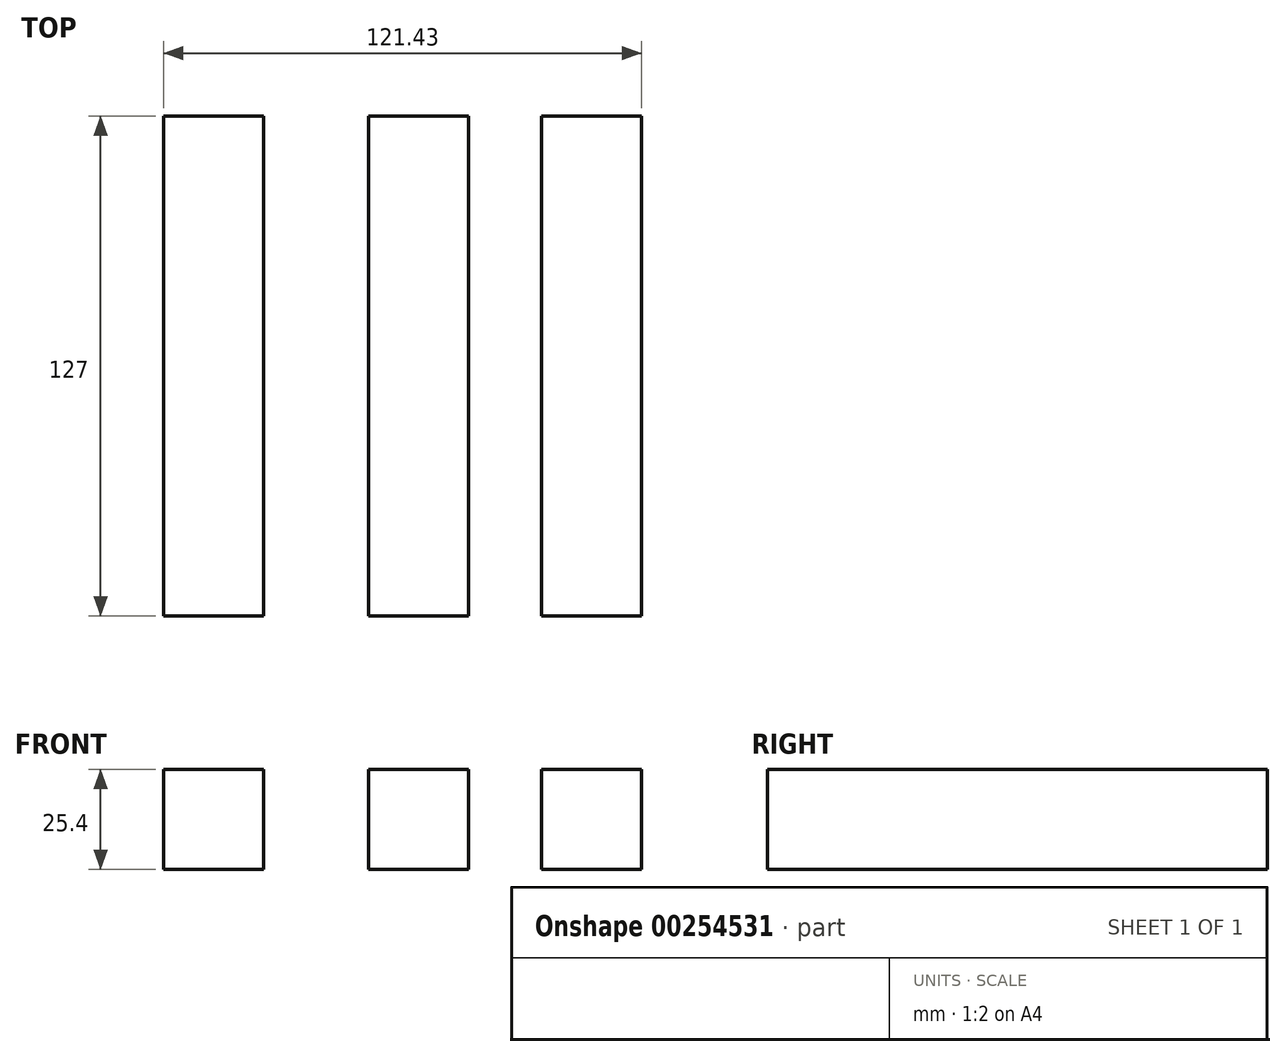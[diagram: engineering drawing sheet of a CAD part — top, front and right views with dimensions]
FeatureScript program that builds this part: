
annotation { "Feature Type Name" : "Feature", "Feature Type Description" : "" }
export const myFeature = defineFeature(function(context is Context, id is Id, definition is map)
    precondition{}
    {
        {
            var Q0;
            Q0=qCreatedBy(makeId("Front.planeOp"),FACE);
            var sketch = newSketch(context, id + "F0", { "sketchPlane" : qUnion([Q0])});
            skLineSegment(sketch, "E0.bottom", {"start": v(12.7, 12.7) * mm, "end": v(-12.7, 12.7) * mm});
            skLineSegment(sketch, "E0.top", {"start": v(12.7, -12.7) * mm, "end": v(-12.7, -12.7) * mm});
            skLineSegment(sketch, "E0.left", {"start": v(12.7, 12.7) * mm, "end": v(12.7, -12.7) * mm});
            skLineSegment(sketch, "E0.right", {"start": v(-12.7, 12.7) * mm, "end": v(-12.7, -12.7) * mm});
            skPoint(sketch, "E0.middle", {"position": v(0, 0) * mm});
            skLineSegment(sketch, "E1.bottom", {"start": v(56.67, 12.7) * mm, "end": v(31.27, 12.7) * mm});
            skLineSegment(sketch, "E1.top", {"start": v(56.67, -12.7) * mm, "end": v(31.27, -12.7) * mm});
            skLineSegment(sketch, "E1.left", {"start": v(56.67, 12.7) * mm, "end": v(56.67, -12.7) * mm});
            skLineSegment(sketch, "E1.right", {"start": v(31.27, 12.7) * mm, "end": v(31.27, -12.7) * mm});
            skPoint(sketch, "E1.middle", {"position": v(43.97, 0) * mm});
            skLineSegment(sketch, "E2.bottom", {"start": v(-39.36, 12.7) * mm, "end": v(-64.76, 12.7) * mm});
            skLineSegment(sketch, "E2.top", {"start": v(-39.36, -12.7) * mm, "end": v(-64.76, -12.7) * mm});
            skLineSegment(sketch, "E2.left", {"start": v(-39.36, 12.7) * mm, "end": v(-39.36, -12.7) * mm});
            skLineSegment(sketch, "E2.right", {"start": v(-64.76, 12.7) * mm, "end": v(-64.76, -12.7) * mm});
            skPoint(sketch, "E2.middle", {"position": v(-52.06, 0) * mm});
            skSolve(sketch);
        }
        {
            var Q0;
            Q0 = qSketchRegion(id + "F0", true);
            extrude(context, id + "F1", {"entities" : qUnion([Q0]), "oppositeDirection" : true, "depth" : 127 * mm});
        }
    });
